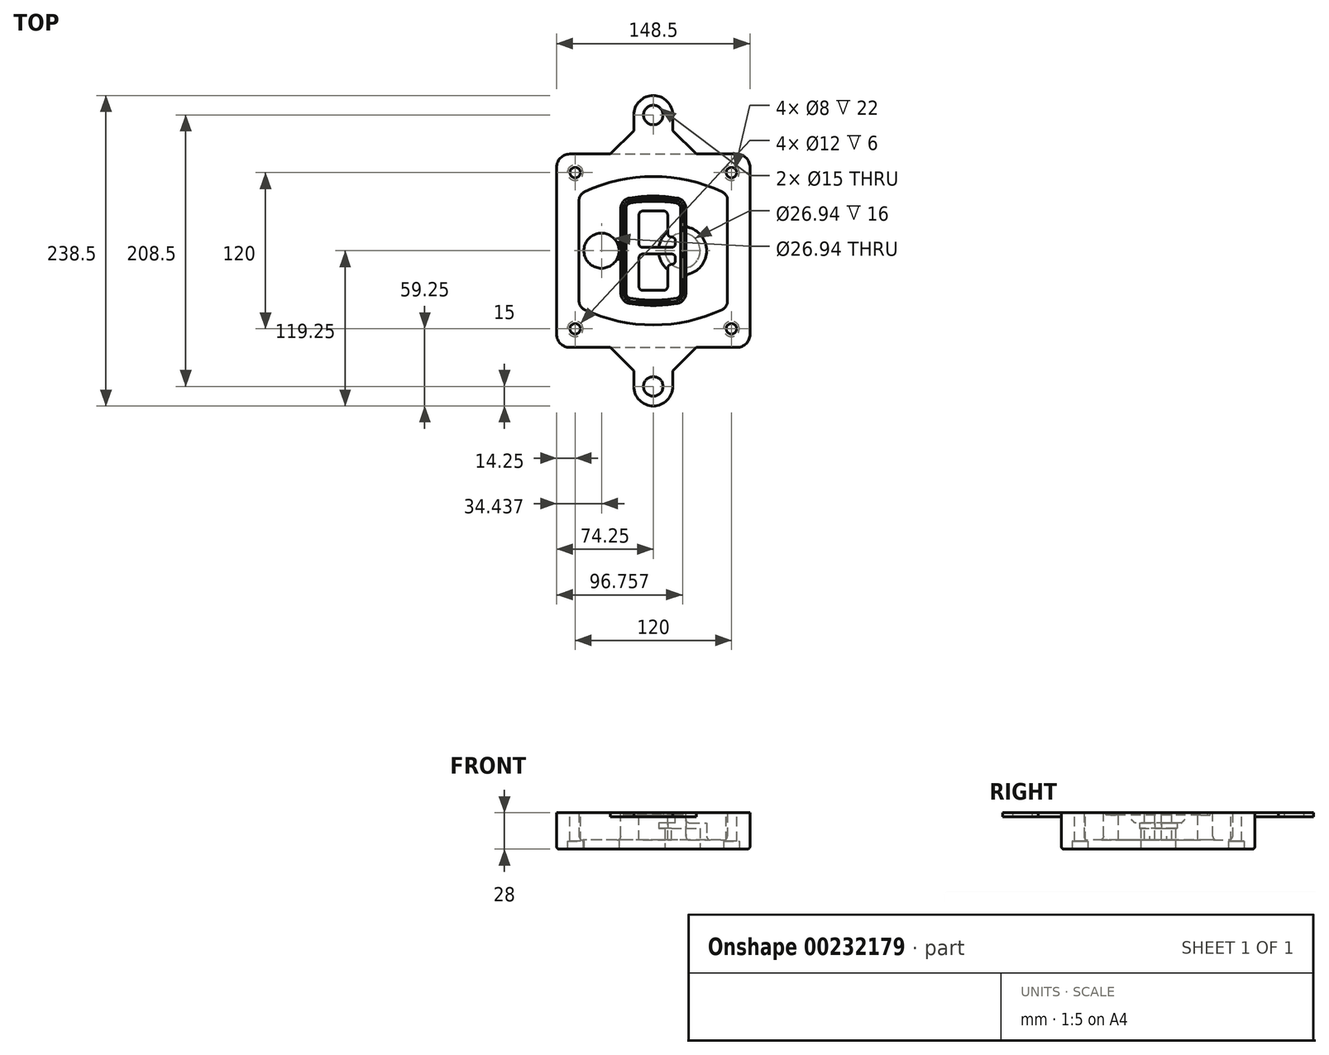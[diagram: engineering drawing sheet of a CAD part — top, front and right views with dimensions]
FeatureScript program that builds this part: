
annotation { "Feature Type Name" : "Feature", "Feature Type Description" : "" }
export const myFeature = defineFeature(function(context is Context, id is Id, definition is map)
    precondition{}
    {
        {
            var Q0;
            Q0=qCreatedBy(makeId("Top.planeOp"),FACE);
            var sketch = newSketch(context, id + "F0", { "sketchPlane" : qUnion([Q0])});
            skPoint(sketch, "E0.rect.middle", {"position": v(0, 0) * mm});
            skLineSegment(sketch, "E1.bottom", {"start": v(-64.25, -74.25) * mm, "end": v(64.25, -74.25) * mm});
            skLineSegment(sketch, "E1.top", {"start": v(-64.25, 74.25) * mm, "end": v(64.25, 74.25) * mm});
            skLineSegment(sketch, "E1.left", {"start": v(-74.25, -64.25) * mm, "end": v(-74.25, 64.25) * mm});
            skLineSegment(sketch, "E1.right", {"start": v(74.25, -64.25) * mm, "end": v(74.25, 64.25) * mm});
            skLineSegment(sketch, "E2", {"start": v(-74.25, 74.25) * mm, "end": v(74.25, -74.25) * mm, "construction": true});
            skLineSegment(sketch, "E3", {"start": v(74.25, 74.25) * mm, "end": v(-74.25, -74.25) * mm, "construction": true});
            skCircle(sketch, "E4", {"center": v(-60, 60) * mm, "radius": 4 * mm});
            skCircle(sketch, "E5", {"center": v(60, 60) * mm, "radius": 4 * mm});
            skCircle(sketch, "E6", {"center": v(60, -60) * mm, "radius": 4 * mm});
            skCircle(sketch, "E7", {"center": v(-60, -60) * mm, "radius": 4 * mm});
            skLineSegment(sketch, "E8", {"start": v(-60, 60) * mm, "end": v(60, 60) * mm, "construction": true});
            skLineSegment(sketch, "E9", {"start": v(60, 60) * mm, "end": v(60, -60) * mm, "construction": true});
            skLineSegment(sketch, "E10", {"start": v(60, -60) * mm, "end": v(-60, -60) * mm, "construction": true});
            skLineSegment(sketch, "E11", {"start": v(-60, -60) * mm, "end": v(-60, 60) * mm, "construction": true});
            skLineSegment(sketch, "E12", {"start": v(-60, 38.83) * mm, "end": v(-60, -38.83) * mm});
            skLineSegment(sketch, "E13", {"start": v(60, 38.83) * mm, "end": v(60, -38.83) * mm});
            skArc(sketch, "E14", {"start": v(54.26, 47.88) * mm, "mid": v(0, 60) * mm, "end": v(-54.26, 47.88) * mm});
            skArc(sketch, "E15", {"start": v(-54.26, -47.88) * mm, "mid": v(0, -60) * mm, "end": v(54.26, -47.88) * mm});
            skLineSegment(sketch, "E16", {"start": v(-60, 0) * mm, "end": v(60, 0) * mm, "construction": true});
            skPoint(sketch, "E17.visualSharp", {"position": v(-60, -45) * mm});
            skArc(sketch, "E17.filletArc", {"start": v(-60, -38.83) * mm, "mid": v(-58.44, -44.2) * mm, "end": v(-54.26, -47.88) * mm});
            skPoint(sketch, "E18.visualSharp", {"position": v(-60, 45) * mm});
            skArc(sketch, "E18.filletArc", {"start": v(-54.26, 47.88) * mm, "mid": v(-58.44, 44.2) * mm, "end": v(-60, 38.83) * mm});
            skPoint(sketch, "E19.visualSharp", {"position": v(60, 45) * mm});
            skArc(sketch, "E19.filletArc", {"start": v(60, 38.83) * mm, "mid": v(58.44, 44.2) * mm, "end": v(54.26, 47.88) * mm});
            skPoint(sketch, "E20.visualSharp", {"position": v(60, -45) * mm});
            skArc(sketch, "E20.filletArc", {"start": v(54.26, -47.88) * mm, "mid": v(58.44, -44.2) * mm, "end": v(60, -38.83) * mm});
            skPoint(sketch, "E21.visualSharp", {"position": v(-74.25, 74.25) * mm});
            skArc(sketch, "E21.filletArc", {"start": v(-64.25, 74.25) * mm, "mid": v(-71.32, 71.32) * mm, "end": v(-74.25, 64.25) * mm});
            skPoint(sketch, "E22.visualSharp", {"position": v(74.25, 74.25) * mm});
            skArc(sketch, "E22.filletArc", {"start": v(74.25, 64.25) * mm, "mid": v(71.32, 71.32) * mm, "end": v(64.25, 74.25) * mm});
            skPoint(sketch, "E23.visualSharp", {"position": v(74.25, -74.25) * mm});
            skArc(sketch, "E23.filletArc", {"start": v(64.25, -74.25) * mm, "mid": v(71.32, -71.32) * mm, "end": v(74.25, -64.25) * mm});
            skPoint(sketch, "E24.visualSharp", {"position": v(-74.25, -74.25) * mm});
            skArc(sketch, "E24.filletArc", {"start": v(-74.25, -64.25) * mm, "mid": v(-71.32, -71.32) * mm, "end": v(-64.25, -74.25) * mm});
            skArc(sketch, "E25.0", {"start": v(57, 38.83) * mm, "mid": v(55.9, 42.58) * mm, "end": v(52.98, 45.17) * mm});
            skLineSegment(sketch, "E25.1", {"start": v(57, 38.83) * mm, "end": v(57, -38.83) * mm});
            skArc(sketch, "E25.2", {"start": v(52.98, -45.17) * mm, "mid": v(55.9, -42.58) * mm, "end": v(57, -38.83) * mm});
            skArc(sketch, "E25.3", {"start": v(-52.98, -45.17) * mm, "mid": v(0, -57) * mm, "end": v(52.98, -45.17) * mm});
            skArc(sketch, "E25.4", {"start": v(-57, -38.83) * mm, "mid": v(-55.9, -42.58) * mm, "end": v(-52.98, -45.17) * mm});
            skArc(sketch, "E25.5", {"start": v(52.98, 45.17) * mm, "mid": v(0, 57) * mm, "end": v(-52.98, 45.17) * mm});
            skLineSegment(sketch, "E25.6", {"start": v(-57, 38.83) * mm, "end": v(-57, -38.83) * mm});
            skArc(sketch, "E25.7", {"start": v(-52.98, 45.17) * mm, "mid": v(-55.9, 42.58) * mm, "end": v(-57, 38.83) * mm});
            skArc(sketch, "E26.0", {"start": v(-55.96, 51.5) * mm, "mid": v(-61.82, 46.33) * mm, "end": v(-64, 38.83) * mm});
            skArc(sketch, "E26.1", {"start": v(55.96, 51.5) * mm, "mid": v(0, 64) * mm, "end": v(-55.96, 51.5) * mm});
            skArc(sketch, "E26.2", {"start": v(64, 38.83) * mm, "mid": v(61.82, 46.33) * mm, "end": v(55.96, 51.5) * mm});
            skLineSegment(sketch, "E26.3", {"start": v(64, 38.83) * mm, "end": v(64, -38.83) * mm});
            skArc(sketch, "E26.4", {"start": v(55.96, -51.5) * mm, "mid": v(61.82, -46.33) * mm, "end": v(64, -38.83) * mm});
            skLineSegment(sketch, "E26.5", {"start": v(-64, 38.83) * mm, "end": v(-64, -38.83) * mm});
            skArc(sketch, "E26.6", {"start": v(-55.96, -51.5) * mm, "mid": v(0, -64) * mm, "end": v(55.96, -51.5) * mm});
            skArc(sketch, "E26.7", {"start": v(-64, -38.83) * mm, "mid": v(-61.82, -46.33) * mm, "end": v(-55.96, -51.5) * mm});
            skSolve(sketch);
        }
        {
            var Q0;
            Q0=makeQuery(id+"F0.imprint","IMPRINT",FACE,{"disambiguationData":[TD([[makeQuery(id+"F0.imprint","IMPRINT",EDGE,{"derivedFrom":sQuery(id+"F0.wireOp",EDGE,"E1.bottom")}),1.0]])]});
            var Q1;
            Q1=makeQuery(id+"F0.imprint","IMPRINT",FACE,{"disambiguationData":[TD([[makeQuery(id+"F0.imprint","IMPRINT",EDGE,{"derivedFrom":sQuery(id+"F0.wireOp",EDGE,"E12")}),1.0]])]});
            var Q2;
            Q2=makeQuery(id+"F0.imprint","IMPRINT",FACE,{"disambiguationData":[TD([[makeQuery(id+"F0.imprint","IMPRINT",EDGE,{"derivedFrom":sQuery(id+"F0.wireOp",EDGE,"E25.0")}),1.0]])]});
            var Q3;
            Q3=makeQuery(id+"F0.imprint","IMPRINT",FACE,{"disambiguationData":[TD([[makeQuery(id+"F0.imprint","IMPRINT",EDGE,{"derivedFrom":sQuery(id+"F0.wireOp",EDGE,"E12")}),-1.0]])]});
            extrude(context, id + "F1", {"entities" : qUnion([Q0, Q1, Q2, Q3]), "oppositeDirection" : true, "depth" : 25 * mm});
        }
        {
            var Q0;
            Q0=makeQuery(id+"F0.imprint","IMPRINT",FACE,{"disambiguationData":[TD([[makeQuery(id+"F0.imprint","IMPRINT",EDGE,{"derivedFrom":sQuery(id+"F0.wireOp",EDGE,"E12")}),1.0]])]});
            extrude(context, id + "F2", {"entities" : qUnion([Q0]), "operationType" : NewBodyOperationType.ADD, "depth" : 3 * mm});
        }
        {
            var Q0;
            Q0=makeQuery(id+"F0.imprint","IMPRINT",FACE,{"disambiguationData":[TD([[makeQuery(id+"F0.imprint","IMPRINT",EDGE,{"derivedFrom":sQuery(id+"F0.wireOp",EDGE,"E25.0")}),1.0]])]});
            extrude(context, id + "F3", {"entities" : qUnion([Q0]), "operationType" : NewBodyOperationType.REMOVE, "oppositeDirection" : true, "depth" : 18 * mm});
        }
        {
            var Q0;
            Q0=makeQuery(id+"F2.opExtrude","CAP_FACE",FACE,{"disambiguationData":[OSD([sQuery(id+"F0.wireOp",EDGE,"E12"),sQuery(id+"F0.wireOp",EDGE,"E13"),sQuery(id+"F0.wireOp",EDGE,"E14"),sQuery(id+"F0.wireOp",EDGE,"E15"),sQuery(id+"F0.wireOp",EDGE,"E17.filletArc"),sQuery(id+"F0.wireOp",EDGE,"E18.filletArc"),sQuery(id+"F0.wireOp",EDGE,"E19.filletArc"),sQuery(id+"F0.wireOp",EDGE,"E20.filletArc"),sQuery(id+"F0.wireOp",EDGE,"E25.0"),sQuery(id+"F0.wireOp",EDGE,"E25.1"),sQuery(id+"F0.wireOp",EDGE,"E25.2"),sQuery(id+"F0.wireOp",EDGE,"E25.3"),sQuery(id+"F0.wireOp",EDGE,"E25.4"),sQuery(id+"F0.wireOp",EDGE,"E25.5"),sQuery(id+"F0.wireOp",EDGE,"E25.6"),sQuery(id+"F0.wireOp",EDGE,"E25.7")])],"isStart":false});
            var sketch = newSketch(context, id + "F4", { "sketchPlane" : qUnion([Q0])});
            skArc(sketch, "E27.0", {"start": v(-18.34, -40.45) * mm, "mid": v(0, -42) * mm, "end": v(18.34, -40.45) * mm});
            skArc(sketch, "E28.0", {"start": v(18.34, 40.45) * mm, "mid": v(0, 42) * mm, "end": v(-18.34, 40.45) * mm});
            skLineSegment(sketch, "E29", {"start": v(-25, 32.57) * mm, "end": v(-25, -32.57) * mm});
            skLineSegment(sketch, "E30", {"start": v(25, 32.57) * mm, "end": v(25, -32.57) * mm});
            skLineSegment(sketch, "E31", {"start": v(-25, 39.1) * mm, "end": v(25, 39.1) * mm, "construction": true});
            skLineSegment(sketch, "E32", {"start": v(-25, -39.1) * mm, "end": v(25, -39.1) * mm, "construction": true});
            skPoint(sketch, "E33.visualSharp", {"position": v(-25, 39.1) * mm});
            skArc(sketch, "E33.filletArc", {"start": v(-18.34, 40.45) * mm, "mid": v(-23.11, 37.73) * mm, "end": v(-25, 32.57) * mm});
            skPoint(sketch, "E34.visualSharp", {"position": v(25, 39.1) * mm});
            skArc(sketch, "E34.filletArc", {"start": v(25, 32.57) * mm, "mid": v(23.11, 37.73) * mm, "end": v(18.34, 40.45) * mm});
            skPoint(sketch, "E35.visualSharp", {"position": v(25, -39.1) * mm});
            skArc(sketch, "E35.filletArc", {"start": v(18.34, -40.45) * mm, "mid": v(23.11, -37.73) * mm, "end": v(25, -32.57) * mm});
            skPoint(sketch, "E36.visualSharp", {"position": v(-25, -39.1) * mm});
            skArc(sketch, "E36.filletArc", {"start": v(-25, -32.57) * mm, "mid": v(-23.11, -37.73) * mm, "end": v(-18.34, -40.45) * mm});
            skArc(sketch, "E37.0", {"start": v(52.98, 45.17) * mm, "mid": v(0, 57) * mm, "end": v(-52.98, 45.17) * mm});
            skArc(sketch, "E37.1", {"start": v(-52.98, 45.17) * mm, "mid": v(-55.9, 42.58) * mm, "end": v(-57, 38.83) * mm});
            skLineSegment(sketch, "E37.2", {"start": v(-57, 38.83) * mm, "end": v(-57, -38.83) * mm});
            skArc(sketch, "E37.3", {"start": v(-57, -38.83) * mm, "mid": v(-55.9, -42.58) * mm, "end": v(-52.98, -45.17) * mm});
            skArc(sketch, "E37.4", {"start": v(-52.98, -45.17) * mm, "mid": v(0, -57) * mm, "end": v(52.98, -45.17) * mm});
            skArc(sketch, "E37.5", {"start": v(52.98, -45.17) * mm, "mid": v(55.9, -42.58) * mm, "end": v(57, -38.83) * mm});
            skLineSegment(sketch, "E37.6", {"start": v(57, 38.83) * mm, "end": v(57, -38.83) * mm});
            skArc(sketch, "E37.7", {"start": v(57, 38.83) * mm, "mid": v(55.9, 42.58) * mm, "end": v(52.98, 45.17) * mm});
            skLineSegment(sketch, "E38.0", {"start": v(23, 32.57) * mm, "end": v(23, -32.57) * mm});
            skArc(sketch, "E38.1", {"start": v(18, -38.48) * mm, "mid": v(21.58, -36.44) * mm, "end": v(23, -32.57) * mm});
            skArc(sketch, "E38.2", {"start": v(-18, -38.48) * mm, "mid": v(0, -40) * mm, "end": v(18, -38.48) * mm});
            skArc(sketch, "E38.3", {"start": v(-23, -32.57) * mm, "mid": v(-21.58, -36.44) * mm, "end": v(-18, -38.48) * mm});
            skLineSegment(sketch, "E38.4", {"start": v(-23, 32.57) * mm, "end": v(-23, -32.57) * mm});
            skArc(sketch, "E38.5", {"start": v(23, 32.57) * mm, "mid": v(21.58, 36.44) * mm, "end": v(18, 38.48) * mm});
            skArc(sketch, "E38.6", {"start": v(-18, 38.48) * mm, "mid": v(-21.58, 36.44) * mm, "end": v(-23, 32.57) * mm});
            skArc(sketch, "E38.7", {"start": v(18, 38.48) * mm, "mid": v(0, 40) * mm, "end": v(-18, 38.48) * mm});
            skArc(sketch, "E39.0", {"start": v(21, 32.57) * mm, "mid": v(20.06, 35.15) * mm, "end": v(17.67, 36.5) * mm});
            skLineSegment(sketch, "E39.1", {"start": v(21, 32.57) * mm, "end": v(21, -32.57) * mm});
            skArc(sketch, "E39.2", {"start": v(17.67, -36.5) * mm, "mid": v(20.06, -35.15) * mm, "end": v(21, -32.57) * mm});
            skArc(sketch, "E39.3", {"start": v(-17.67, -36.5) * mm, "mid": v(0, -38) * mm, "end": v(17.67, -36.5) * mm});
            skArc(sketch, "E39.4", {"start": v(-21, -32.57) * mm, "mid": v(-20.06, -35.15) * mm, "end": v(-17.67, -36.5) * mm});
            skArc(sketch, "E39.5", {"start": v(17.67, 36.5) * mm, "mid": v(0, 38) * mm, "end": v(-17.67, 36.5) * mm});
            skLineSegment(sketch, "E39.6", {"start": v(-21, 32.57) * mm, "end": v(-21, -32.57) * mm});
            skArc(sketch, "E39.7", {"start": v(-17.67, 36.5) * mm, "mid": v(-20.06, 35.15) * mm, "end": v(-21, 32.57) * mm});
            skLineSegment(sketch, "E40", {"start": v(-25, 0) * mm, "end": v(25, 0) * mm, "construction": true});
            skLineSegment(sketch, "E41", {"start": v(-11, 5.5) * mm, "end": v(-11, 27.5) * mm});
            skLineSegment(sketch, "E42", {"start": v(-8, 30.5) * mm, "end": v(8, 30.5) * mm});
            skLineSegment(sketch, "E43", {"start": v(11, 27.5) * mm, "end": v(11, 13.5) * mm});
            skLineSegment(sketch, "E44", {"start": v(14, 10.5) * mm, "end": v(14, 10.5) * mm});
            skLineSegment(sketch, "E45", {"start": v(17, 7.5) * mm, "end": v(17, 5.5) * mm});
            skLineSegment(sketch, "E46", {"start": v(14, 2.5) * mm, "end": v(-8, 2.5) * mm});
            skPoint(sketch, "E47.visualSharp", {"position": v(-11, 30.5) * mm});
            skArc(sketch, "E47.filletArc", {"start": v(-8, 30.5) * mm, "mid": v(-10.12, 29.62) * mm, "end": v(-11, 27.5) * mm});
            skPoint(sketch, "E48.visualSharp", {"position": v(11, 30.5) * mm});
            skArc(sketch, "E48.filletArc", {"start": v(11, 27.5) * mm, "mid": v(10.12, 29.62) * mm, "end": v(8, 30.5) * mm});
            skPoint(sketch, "E49.visualSharp", {"position": v(11, 10.5) * mm});
            skArc(sketch, "E49.filletArc", {"start": v(11, 13.5) * mm, "mid": v(11.88, 11.38) * mm, "end": v(14, 10.5) * mm});
            skPoint(sketch, "E50.visualSharp", {"position": v(17, 10.5) * mm});
            skArc(sketch, "E50.filletArc", {"start": v(17, 7.5) * mm, "mid": v(16.12, 9.62) * mm, "end": v(14, 10.5) * mm});
            skPoint(sketch, "E51.visualSharp", {"position": v(17, 2.5) * mm});
            skArc(sketch, "E51.filletArc", {"start": v(14, 2.5) * mm, "mid": v(16.12, 3.38) * mm, "end": v(17, 5.5) * mm});
            skPoint(sketch, "E52.visualSharp", {"position": v(-11, 2.5) * mm});
            skArc(sketch, "E52.filletArc", {"start": v(-11, 5.5) * mm, "mid": v(-10.12, 3.38) * mm, "end": v(-8, 2.5) * mm});
            skLineSegment(sketch, "E53.0.MirrorCS", {"start": v(14, -2.5) * mm, "end": v(-8, -2.5) * mm});
            skArc(sketch, "E54.0.MirrorCS", {"start": v(-11, -5.5) * mm, "mid": v(-10.12, -3.38) * mm, "end": v(-8, -2.5) * mm});
            skLineSegment(sketch, "E55.0.MirrorCS", {"start": v(-11, -5.5) * mm, "end": v(-11, -27.5) * mm});
            skArc(sketch, "E56.0.MirrorCS", {"start": v(-8, -30.5) * mm, "mid": v(-10.12, -29.62) * mm, "end": v(-11, -27.5) * mm});
            skLineSegment(sketch, "E57.0.MirrorCS", {"start": v(-8, -30.5) * mm, "end": v(8, -30.5) * mm});
            skArc(sketch, "E58.0.MirrorCS", {"start": v(11, -27.5) * mm, "mid": v(10.12, -29.62) * mm, "end": v(8, -30.5) * mm});
            skLineSegment(sketch, "E59.0.MirrorCS", {"start": v(11, -27.5) * mm, "end": v(11, -13.5) * mm});
            skArc(sketch, "E60.0.MirrorCS", {"start": v(11, -13.5) * mm, "mid": v(11.88, -11.38) * mm, "end": v(14, -10.5) * mm});
            skArc(sketch, "E61.0.MirrorCS", {"start": v(17, -7.5) * mm, "mid": v(16.12, -9.62) * mm, "end": v(14, -10.5) * mm});
            skLineSegment(sketch, "E62.0.MirrorCS", {"start": v(17, -7.5) * mm, "end": v(17, -5.5) * mm});
            skArc(sketch, "E63.0.MirrorCS", {"start": v(14, -2.5) * mm, "mid": v(16.12, -3.38) * mm, "end": v(17, -5.5) * mm});
            skSolve(sketch);
        }
        {
            var Q0;
            Q0=makeQuery(id+"F4.imprint","IMPRINT",FACE,{"disambiguationData":[TD([[makeQuery(id+"F4.imprint","IMPRINT",EDGE,{"derivedFrom":sQuery(id+"F4.wireOp",EDGE,"E27.0")}),1.0]])]});
            var Q1;
            Q1=makeQuery(id+"F4.imprint","IMPRINT",FACE,{"disambiguationData":[TD([[makeQuery(id+"F4.imprint","IMPRINT",EDGE,{"derivedFrom":sQuery(id+"F4.wireOp",EDGE,"E38.0")}),-1.0]])]});
            var Q2;
            Q2=makeQuery(id+"F4.imprint","IMPRINT",FACE,{"disambiguationData":[TD([[makeQuery(id+"F4.imprint","IMPRINT",EDGE,{"derivedFrom":sQuery(id+"F4.wireOp",EDGE,"E39.0")}),1.0]])]});
            extrude(context, id + "F5", {"entities" : qUnion([Q0, Q1, Q2]), "operationType" : NewBodyOperationType.ADD, "endBound" : BoundingType.UP_TO_NEXT, "oppositeDirection" : true, "depth" : 25 * mm});
        }
        {
            var Q0;
            Q0=makeQuery(id+"F4.imprint","IMPRINT",FACE,{"disambiguationData":[TD([[makeQuery(id+"F4.imprint","IMPRINT",EDGE,{"derivedFrom":sQuery(id+"F4.wireOp",EDGE,"E38.0")}),-1.0]])]});
            extrude(context, id + "F6", {"entities" : qUnion([Q0]), "operationType" : NewBodyOperationType.REMOVE, "oppositeDirection" : true, "depth" : 2 * mm});
        }
        {
            var Q0;
            Q0=makeQuery(id+"F1.opExtrude","CAP_FACE",FACE,{"disambiguationData":[OSD([sQuery(id+"F0.wireOp",EDGE,"E1.bottom"),sQuery(id+"F0.wireOp",EDGE,"E1.top"),sQuery(id+"F0.wireOp",EDGE,"E1.left"),sQuery(id+"F0.wireOp",EDGE,"E1.right"),sQuery(id+"F0.wireOp",EDGE,"E4"),sQuery(id+"F0.wireOp",EDGE,"E5"),sQuery(id+"F0.wireOp",EDGE,"E6"),sQuery(id+"F0.wireOp",EDGE,"E7"),sQuery(id+"F0.wireOp",EDGE,"E21.filletArc"),sQuery(id+"F0.wireOp",EDGE,"E22.filletArc"),sQuery(id+"F0.wireOp",EDGE,"E23.filletArc"),sQuery(id+"F0.wireOp",EDGE,"E24.filletArc")])],"isStart":false});
            var sketch = newSketch(context, id + "F7", { "sketchPlane" : qUnion([Q0])});
            skCircle(sketch, "E64", {"center": v(22.5, 0) * mm, "radius": 13.47 * mm});
            skCircle(sketch, "E65", {"center": v(-39.81, 0) * mm, "radius": 13.47 * mm});
            skLineSegment(sketch, "E66", {"start": v(74.25, 0) * mm, "end": v(-74.25, 0) * mm});
            skCircle(sketch, "E67", {"center": v(22.5, 0) * mm, "radius": 18.47 * mm});
            skCircle(sketch, "E68", {"center": v(60, -60) * mm, "radius": 6 * mm});
            skCircle(sketch, "E69", {"center": v(-60, -60) * mm, "radius": 6 * mm});
            skCircle(sketch, "E70", {"center": v(-60, 60) * mm, "radius": 6 * mm});
            skCircle(sketch, "E71", {"center": v(60, 60) * mm, "radius": 6 * mm});
            skSolve(sketch);
        }
        {
            var Q0;
            {var subQ1=sQuery(id+"F7.wireOp",EDGE,"E66");var subQ4=sQuery(id+"F7.wireOp",EDGE,"E64");var subQ6=makeQuery(id+"F7.imprint","INTERSECT",VERTEX,{"disambiguationData":[OD(0.0)],"derivedFrom":[subQ4,subQ1]});Q0=makeQuery(id+"F7.imprint","IMPRINT",FACE,{"disambiguationData":[TD([[makeQuery(id+"F7.imprint","IMPRINT",EDGE,{"disambiguationData":[TD([[subQ6,-1.0]])],"derivedFrom":subQ4}),-1.0]])]});}
            var Q1;
            {var subQ0=sQuery(id+"F7.wireOp",EDGE,"E66");var subQ1=sQuery(id+"F7.wireOp",EDGE,"E64");var subQ3=makeQuery(id+"F7.imprint","INTERSECT",VERTEX,{"disambiguationData":[OD(0.0)],"derivedFrom":[subQ1,subQ0]});Q1=makeQuery(id+"F7.imprint","IMPRINT",FACE,{"disambiguationData":[TD([[makeQuery(id+"F7.imprint","IMPRINT",EDGE,{"disambiguationData":[TD([[subQ3,-1.0]])],"derivedFrom":subQ1}),1.0]])]});}
            var Q2;
            {var subQ0=sQuery(id+"F7.wireOp",EDGE,"E66");var subQ1=sQuery(id+"F7.wireOp",EDGE,"E64");var subQ3=makeQuery(id+"F7.imprint","INTERSECT",VERTEX,{"disambiguationData":[OD(0.0)],"derivedFrom":[subQ1,subQ0]});Q2=makeQuery(id+"F7.imprint","IMPRINT",FACE,{"disambiguationData":[TD([[makeQuery(id+"F7.imprint","IMPRINT",EDGE,{"disambiguationData":[TD([[subQ3,1.0]])],"derivedFrom":subQ1}),1.0]])]});}
            var Q3;
            {var subQ1=sQuery(id+"F7.wireOp",EDGE,"E66");var subQ4=sQuery(id+"F7.wireOp",EDGE,"E64");var subQ6=makeQuery(id+"F7.imprint","INTERSECT",VERTEX,{"disambiguationData":[OD(0.0)],"derivedFrom":[subQ4,subQ1]});Q3=makeQuery(id+"F7.imprint","IMPRINT",FACE,{"disambiguationData":[TD([[makeQuery(id+"F7.imprint","IMPRINT",EDGE,{"disambiguationData":[TD([[subQ6,1.0]])],"derivedFrom":subQ4}),-1.0]])]});}
            extrude(context, id + "F8", {"entities" : qUnion([Q0, Q1, Q2, Q3]), "operationType" : NewBodyOperationType.ADD, "oppositeDirection" : true, "depth" : 20 * mm});
        }
        {
            var Q0;
            {var subQ0=sQuery(id+"F7.wireOp",EDGE,"E66");var subQ1=sQuery(id+"F7.wireOp",EDGE,"E64");var subQ3=makeQuery(id+"F7.imprint","INTERSECT",VERTEX,{"disambiguationData":[OD(0.0)],"derivedFrom":[subQ1,subQ0]});Q0=makeQuery(id+"F7.imprint","IMPRINT",FACE,{"disambiguationData":[TD([[makeQuery(id+"F7.imprint","IMPRINT",EDGE,{"disambiguationData":[TD([[subQ3,-1.0]])],"derivedFrom":subQ1}),1.0]])]});}
            var Q1;
            {var subQ0=sQuery(id+"F7.wireOp",EDGE,"E66");var subQ1=sQuery(id+"F7.wireOp",EDGE,"E64");var subQ3=makeQuery(id+"F7.imprint","INTERSECT",VERTEX,{"disambiguationData":[OD(0.0)],"derivedFrom":[subQ1,subQ0]});Q1=makeQuery(id+"F7.imprint","IMPRINT",FACE,{"disambiguationData":[TD([[makeQuery(id+"F7.imprint","IMPRINT",EDGE,{"disambiguationData":[TD([[subQ3,1.0]])],"derivedFrom":subQ1}),1.0]])]});}
            extrude(context, id + "F9", {"entities" : qUnion([Q0, Q1]), "operationType" : NewBodyOperationType.REMOVE, "oppositeDirection" : true, "depth" : 16 * mm});
        }
        {
            var Q0;
            {var subQ0=sQuery(id+"F7.wireOp",EDGE,"E66");var subQ1=sQuery(id+"F7.wireOp",EDGE,"E65");var subQ3=makeQuery(id+"F7.imprint","INTERSECT",VERTEX,{"disambiguationData":[OD(0.0)],"derivedFrom":[subQ1,subQ0]});Q0=makeQuery(id+"F7.imprint","IMPRINT",FACE,{"disambiguationData":[TD([[makeQuery(id+"F7.imprint","IMPRINT",EDGE,{"disambiguationData":[TD([[subQ3,-1.0]])],"derivedFrom":subQ1}),1.0]])]});}
            var Q1;
            {var subQ0=sQuery(id+"F7.wireOp",EDGE,"E66");var subQ1=sQuery(id+"F7.wireOp",EDGE,"E65");var subQ3=makeQuery(id+"F7.imprint","INTERSECT",VERTEX,{"disambiguationData":[OD(0.0)],"derivedFrom":[subQ1,subQ0]});Q1=makeQuery(id+"F7.imprint","IMPRINT",FACE,{"disambiguationData":[TD([[makeQuery(id+"F7.imprint","IMPRINT",EDGE,{"disambiguationData":[TD([[subQ3,1.0]])],"derivedFrom":subQ1}),1.0]])]});}
            extrude(context, id + "F10", {"entities" : qUnion([Q0, Q1]), "operationType" : NewBodyOperationType.REMOVE, "oppositeDirection" : true, "depth" : 25 * mm});
        }
        {
            var Q0;
            Q0=makeQuery(id+"F7.imprint","IMPRINT",FACE,{"disambiguationData":[TD([[makeQuery(id+"F7.imprint","IMPRINT",EDGE,{"derivedFrom":sQuery(id+"F7.wireOp",EDGE,"E68")}),1.0]])]});
            var Q1;
            Q1=makeQuery(id+"F7.imprint","IMPRINT",FACE,{"disambiguationData":[TD([[makeQuery(id+"F7.imprint","IMPRINT",EDGE,{"derivedFrom":makeQuery(id+"F1.opExtrude","CAP_EDGE",EDGE,{"disambiguationData":[OSD([sQuery(id+"F0.wireOp",EDGE,"E5")])],"isStart":false})}),-1.0]])]});
            var Q2;
            Q2=makeQuery(id+"F7.imprint","IMPRINT",FACE,{"disambiguationData":[TD([[makeQuery(id+"F7.imprint","IMPRINT",EDGE,{"derivedFrom":sQuery(id+"F7.wireOp",EDGE,"E69")}),1.0]])]});
            var Q3;
            Q3=makeQuery(id+"F7.imprint","IMPRINT",FACE,{"disambiguationData":[TD([[makeQuery(id+"F7.imprint","IMPRINT",EDGE,{"derivedFrom":makeQuery(id+"F1.opExtrude","CAP_EDGE",EDGE,{"disambiguationData":[OSD([sQuery(id+"F0.wireOp",EDGE,"E4")])],"isStart":false})}),-1.0]])]});
            var Q4;
            Q4=makeQuery(id+"F7.imprint","IMPRINT",FACE,{"disambiguationData":[TD([[makeQuery(id+"F7.imprint","IMPRINT",EDGE,{"derivedFrom":sQuery(id+"F7.wireOp",EDGE,"E70")}),1.0]])]});
            var Q5;
            Q5=makeQuery(id+"F7.imprint","IMPRINT",FACE,{"disambiguationData":[TD([[makeQuery(id+"F7.imprint","IMPRINT",EDGE,{"derivedFrom":makeQuery(id+"F1.opExtrude","CAP_EDGE",EDGE,{"disambiguationData":[OSD([sQuery(id+"F0.wireOp",EDGE,"E7")])],"isStart":false})}),-1.0]])]});
            var Q6;
            Q6=makeQuery(id+"F7.imprint","IMPRINT",FACE,{"disambiguationData":[TD([[makeQuery(id+"F7.imprint","IMPRINT",EDGE,{"derivedFrom":sQuery(id+"F7.wireOp",EDGE,"E71")}),1.0]])]});
            var Q7;
            Q7=makeQuery(id+"F7.imprint","IMPRINT",FACE,{"disambiguationData":[TD([[makeQuery(id+"F7.imprint","IMPRINT",EDGE,{"derivedFrom":makeQuery(id+"F1.opExtrude","CAP_EDGE",EDGE,{"disambiguationData":[OSD([sQuery(id+"F0.wireOp",EDGE,"E6")])],"isStart":false})}),-1.0]])]});
            extrude(context, id + "F11", {"entities" : qUnion([Q0, Q1, Q2, Q3, Q4, Q5, Q6, Q7]), "operationType" : NewBodyOperationType.REMOVE, "oppositeDirection" : true, "depth" : 6 * mm});
        }
        {
            var Q0;
            Q0=makeQuery(id+"F9.boolean.opBoolean","COPY",FACE,{"derivedFrom":makeQuery(id+"F9.opExtrude","CAP_FACE",FACE,{"disambiguationData":[OSD([sQuery(id+"F7.wireOp",EDGE,"E64")])],"isStart":false})});
            var sketch = newSketch(context, id + "F12", { "sketchPlane" : qUnion([Q0])});
            skArc(sketch, "E72.0", {"start": v(11, 14.45) * mm, "mid": v(6.45, 9.13) * mm, "end": v(4.2, 2.5) * mm});
            skArc(sketch, "E72.1", {"start": v(4.2, -2.5) * mm, "mid": v(6.45, -9.13) * mm, "end": v(11, -14.45) * mm});
            skLineSegment(sketch, "E73", {"start": v(4.2, -2.5) * mm, "end": v(14, -2.5) * mm});
            skLineSegment(sketch, "E74.0", {"start": v(14, 2.5) * mm, "end": v(4.2, 2.5) * mm});
            skArc(sketch, "E74.1", {"start": v(14, 2.5) * mm, "mid": v(16.12, 3.38) * mm, "end": v(17, 5.5) * mm});
            skLineSegment(sketch, "E74.2", {"start": v(17, 7.5) * mm, "end": v(17, 5.5) * mm});
            skArc(sketch, "E74.3", {"start": v(17, 7.5) * mm, "mid": v(16.12, 9.62) * mm, "end": v(14, 10.5) * mm});
            skArc(sketch, "E74.4", {"start": v(11, 13.5) * mm, "mid": v(11.88, 11.38) * mm, "end": v(14, 10.5) * mm});
            skLineSegment(sketch, "E74.5", {"start": v(11, 14.45) * mm, "end": v(11, 13.5) * mm});
            skLineSegment(sketch, "E74.7", {"start": v(14, -2.5) * mm, "end": v(4.2, -2.5) * mm});
            skArc(sketch, "E74.8", {"start": v(14, -2.5) * mm, "mid": v(16.12, -3.38) * mm, "end": v(17, -5.5) * mm});
            skLineSegment(sketch, "E74.9", {"start": v(17, -7.5) * mm, "end": v(17, -5.5) * mm});
            skArc(sketch, "E74.10", {"start": v(17, -7.5) * mm, "mid": v(16.12, -9.62) * mm, "end": v(14, -10.5) * mm});
            skArc(sketch, "E74.11", {"start": v(11, -13.5) * mm, "mid": v(11.88, -11.38) * mm, "end": v(14, -10.5) * mm});
            skLineSegment(sketch, "E74.12", {"start": v(11, -14.45) * mm, "end": v(11, -13.5) * mm});
            skPoint(sketch, "E75.orphan", {"position": v(11, -27.5) * mm});
            skPoint(sketch, "E76.orphan", {"position": v(-8, -2.5) * mm});
            skPoint(sketch, "E77.orphan", {"position": v(-8, 2.5) * mm});
            skPoint(sketch, "E78.orphan", {"position": v(11, 27.5) * mm});
            skSolve(sketch);
        }
        {
            var Q0;
            {var subQ7=sQuery(id+"F12.wireOp",EDGE,"E72.0");var subQ14=sQuery(id+"F12.wireOp",EDGE,"E72.1");var subQ16=sQuery(id+"F12.wireOp",EDGE,"E74.1");var subQ18=sQuery(id+"F12.wireOp",EDGE,"E74.8");Q0=qUnion([makeQuery(id+"F12.imprint","IMPRINT",FACE,{"disambiguationData":[TD([[makeQuery(id+"F12.imprint","IMPRINT",EDGE,{"derivedFrom":subQ7}),1.0]])]}),makeQuery(id+"F12.imprint","IMPRINT",FACE,{"disambiguationData":[TD([[makeQuery(id+"F12.imprint","IMPRINT",EDGE,{"derivedFrom":subQ14}),1.0]])]}),makeQuery(id+"F12.imprint","IMPRINT",FACE,{"disambiguationData":[TD([[makeQuery(id+"F12.imprint","IMPRINT",EDGE,{"derivedFrom":subQ16}),1.0]])]}),makeQuery(id+"F12.imprint","IMPRINT",FACE,{"disambiguationData":[TD([[makeQuery(id+"F12.imprint","IMPRINT",EDGE,{"derivedFrom":subQ18}),-1.0]])]})]);}
            var Q1;
            Q1=makeQuery(id+"F5.boolean.opBoolean","SPLIT",FACE,{"disambiguationData":[TD([makeQuery(id+"F5.opExtrude","SWEPT_FACE",FACE,{"disambiguationData":[OSD([sQuery(id+"F4.wireOp",EDGE,"E41")])]})])],"derivedFrom":makeQuery(id+"F3.boolean.opBoolean","COPY",FACE,{"derivedFrom":makeQuery(id+"F3.opExtrude","CAP_FACE",FACE,{"disambiguationData":[OSD([sQuery(id+"F0.wireOp",EDGE,"E25.0"),sQuery(id+"F0.wireOp",EDGE,"E25.1"),sQuery(id+"F0.wireOp",EDGE,"E25.2"),sQuery(id+"F0.wireOp",EDGE,"E25.3"),sQuery(id+"F0.wireOp",EDGE,"E25.4"),sQuery(id+"F0.wireOp",EDGE,"E25.5"),sQuery(id+"F0.wireOp",EDGE,"E25.6"),sQuery(id+"F0.wireOp",EDGE,"E25.7")])],"isStart":false})})});
            extrude(context, id + "F13", {"entities" : qUnion([Q0]), "operationType" : NewBodyOperationType.REMOVE, "endBound" : BoundingType.UP_TO_SURFACE, "endBoundEntityFace" : qUnion([Q1]), "depth" : 25 * mm});
        }
        {
            var Q0;
            Q0=makeQuery(id+"F3.boolean.opBoolean","COPY",EDGE,{"derivedFrom":makeQuery(id+"F3.opExtrude","CAP_EDGE",EDGE,{"disambiguationData":[OSD([sQuery(id+"F0.wireOp",EDGE,"E25.6")])],"isStart":false})});
            var Q1;
            Q1=makeQuery(id+"F8.boolean.opBoolean","INTERSECT",EDGE,{"derivedFrom":[makeQuery(id+"F5.opExtrude","SWEPT_FACE",FACE,{"disambiguationData":[OSD([sQuery(id+"F4.wireOp",EDGE,"E30")])]}),makeQuery(id+"F8.opExtrude","CAP_FACE",FACE,{"disambiguationData":[OSD([sQuery(id+"F7.wireOp",EDGE,"E67")])],"isStart":false})]});
            var Q2;
            Q2=makeQuery(id+"F8.boolean.opBoolean","INTERSECT",EDGE,{"disambiguationData":[OD(1.0)],"derivedFrom":[makeQuery(id+"F5.opExtrude","SWEPT_FACE",FACE,{"disambiguationData":[OSD([sQuery(id+"F4.wireOp",EDGE,"E30")])]}),makeQuery(id+"F8.opExtrude","SWEPT_FACE",FACE,{"disambiguationData":[OSD([sQuery(id+"F7.wireOp",EDGE,"E67")])]})]});
            var Q3;
            {var subQ0=sQuery(id+"F4.wireOp",EDGE,"E30");Q3=makeQuery(id+"F8.boolean.opBoolean","SPLIT",EDGE,{"disambiguationData":[TD([makeQuery(id+"F5.opExtrude","SWEPT_FACE",FACE,{"disambiguationData":[OSD([sQuery(id+"F4.wireOp",EDGE,"E35.filletArc")])]})])],"derivedFrom":makeQuery(id+"F5.opExtrude","CAP_EDGE",EDGE,{"disambiguationData":[OSD([subQ0])],"isStart":false})});}
            var Q4;
            {var subQ0=sQuery(id+"F0.wireOp",EDGE,"E25.7");var subQ1=sQuery(id+"F0.wireOp",EDGE,"E25.1");var subQ2=sQuery(id+"F0.wireOp",EDGE,"E25.6");var subQ3=sQuery(id+"F0.wireOp",EDGE,"E25.5");var subQ4=sQuery(id+"F0.wireOp",EDGE,"E25.4");var subQ5=sQuery(id+"F0.wireOp",EDGE,"E25.0");var subQ6=sQuery(id+"F0.wireOp",EDGE,"E25.2");var subQ7=sQuery(id+"F0.wireOp",EDGE,"E25.3");Q4=makeQuery(id+"F8.boolean.opBoolean","INTERSECT",EDGE,{"derivedFrom":[makeQuery(id+"F5.boolean.opBoolean","SPLIT",FACE,{"disambiguationData":[TD([makeQuery(id+"F2.opExtrude","SWEPT_FACE",FACE,{"disambiguationData":[OSD([subQ5])]})])],"derivedFrom":makeQuery(id+"F3.boolean.opBoolean","COPY",FACE,{"derivedFrom":makeQuery(id+"F3.opExtrude","CAP_FACE",FACE,{"disambiguationData":[OSD([subQ5,subQ1,subQ6,subQ7,subQ4,subQ3,subQ2,subQ0])],"isStart":false})})}),makeQuery(id+"F8.opExtrude","SWEPT_FACE",FACE,{"disambiguationData":[OSD([sQuery(id+"F7.wireOp",EDGE,"E67")])]})]});}
            var Q5;
            Q5=makeQuery(id+"F8.boolean.opBoolean","INTERSECT",EDGE,{"disambiguationData":[OD(0.0)],"derivedFrom":[makeQuery(id+"F5.opExtrude","SWEPT_FACE",FACE,{"disambiguationData":[OSD([sQuery(id+"F4.wireOp",EDGE,"E30")])]}),makeQuery(id+"F8.opExtrude","SWEPT_FACE",FACE,{"disambiguationData":[OSD([sQuery(id+"F7.wireOp",EDGE,"E67")])]})]});
            fillet(context, id + "F14", {"entities" : qUnion([Q0, Q1, Q2, Q3, Q4, Q5]), "radius" : 3 * mm, "tangentPropagation" : true, "allowEdgeOverflow" : false});
        }
        {
            var Q0;
            Q0=makeQuery(id+"F1.opExtrude","CAP_EDGE",EDGE,{"disambiguationData":[OSD([sQuery(id+"F0.wireOp",EDGE,"E1.bottom")])],"isStart":false});
            fillet(context, id + "F15", {"entities" : qUnion([Q0]), "radius" : 2 * mm, "tangentPropagation" : true, "allowEdgeOverflow" : false});
        }
        {
            var Q0;
            {var subQ0=sQuery(id+"F0.wireOp",EDGE,"E22.filletArc");var subQ1=sQuery(id+"F0.wireOp",EDGE,"E7");var subQ2=sQuery(id+"F0.wireOp",EDGE,"E6");var subQ3=sQuery(id+"F0.wireOp",EDGE,"E5");var subQ4=sQuery(id+"F0.wireOp",EDGE,"E4");var subQ5=sQuery(id+"F0.wireOp",EDGE,"E1.bottom");var subQ6=sQuery(id+"F0.wireOp",EDGE,"E21.filletArc");var subQ7=sQuery(id+"F0.wireOp",EDGE,"E1.top");var subQ8=sQuery(id+"F0.wireOp",EDGE,"E1.left");var subQ9=sQuery(id+"F0.wireOp",EDGE,"E1.right");var subQ10=sQuery(id+"F0.wireOp",EDGE,"E23.filletArc");var subQ11=sQuery(id+"F0.wireOp",EDGE,"E24.filletArc");Q0=makeQuery(id+"F2.boolean.opBoolean","SPLIT",FACE,{"disambiguationData":[TD([makeQuery(id+"F1.opExtrude","SWEPT_FACE",FACE,{"disambiguationData":[OSD([subQ5])]})])],"derivedFrom":makeQuery(id+"F1.opExtrude","CAP_FACE",FACE,{"disambiguationData":[OSD([subQ5,subQ7,subQ8,subQ9,subQ4,subQ3,subQ2,subQ1,subQ6,subQ0,subQ10,subQ11])],"isStart":true})});}
            var sketch = newSketch(context, id + "F16", { "sketchPlane" : qUnion([Q0])});
            skPoint(sketch, "E79.0", {"position": v(-60, 38.83) * mm});
            skCircle(sketch, "E80.0", {"center": v(-60, 60) * mm, "radius": 4 * mm});
            skLineSegment(sketch, "E81.0.0", {"start": v(64.25, 74.25) * mm, "end": v(-64.25, 74.25) * mm});
            skArc(sketch, "E81.0.1", {"start": v(-64.25, 74.25) * mm, "mid": v(-71.32, 71.32) * mm, "end": v(-74.25, 64.25) * mm});
            skLineSegment(sketch, "E81.0.2", {"start": v(-74.25, 64.25) * mm, "end": v(-74.25, -64.25) * mm});
            skArc(sketch, "E81.0.3", {"start": v(-74.25, -64.25) * mm, "mid": v(-71.32, -71.32) * mm, "end": v(-64.25, -74.25) * mm});
            skLineSegment(sketch, "E81.0.4", {"start": v(-64.25, -74.25) * mm, "end": v(64.25, -74.25) * mm});
            skArc(sketch, "E81.0.5", {"start": v(64.25, -74.25) * mm, "mid": v(71.32, -71.32) * mm, "end": v(74.25, -64.25) * mm});
            skLineSegment(sketch, "E81.0.6", {"start": v(74.25, -64.25) * mm, "end": v(74.25, 64.25) * mm});
            skArc(sketch, "E81.0.7", {"start": v(74.25, 64.25) * mm, "mid": v(71.32, 71.32) * mm, "end": v(64.25, 74.25) * mm});
            skPoint(sketch, "E82.0", {"position": v(0, 60) * mm});
            skArc(sketch, "E83.0.0", {"start": v(51.7, -42.45) * mm, "mid": v(53.38, -40.97) * mm, "end": v(54, -38.83) * mm});
            skLineSegment(sketch, "E83.0.1", {"start": v(54, -38.83) * mm, "end": v(54, 38.83) * mm});
            skArc(sketch, "E83.0.2", {"start": v(54, 38.83) * mm, "mid": v(53.38, 40.97) * mm, "end": v(51.7, 42.45) * mm});
            skArc(sketch, "E83.0.3", {"start": v(51.7, 42.45) * mm, "mid": v(0, 54) * mm, "end": v(-51.7, 42.45) * mm});
            skArc(sketch, "E83.0.4", {"start": v(-51.7, 42.45) * mm, "mid": v(-53.38, 40.97) * mm, "end": v(-54, 38.83) * mm});
            skLineSegment(sketch, "E83.0.5", {"start": v(-54, 38.83) * mm, "end": v(-54, -38.83) * mm});
            skArc(sketch, "E83.0.6", {"start": v(-54, -38.83) * mm, "mid": v(-53.38, -40.97) * mm, "end": v(-51.7, -42.45) * mm});
            skArc(sketch, "E83.0.7", {"start": v(-51.7, -42.45) * mm, "mid": v(0, -54) * mm, "end": v(51.7, -42.45) * mm});
            skCircle(sketch, "E84.2", {"center": v(-60, -60) * mm, "radius": 4 * mm});
            skArc(sketch, "E85.0", {"start": v(-54.26, -47.88) * mm, "mid": v(0, -60) * mm, "end": v(54.26, -47.88) * mm});
            skArc(sketch, "E85.1", {"start": v(-52.98, -45.17) * mm, "mid": v(0, -57) * mm, "end": v(52.98, -45.17) * mm});
            skArc(sketch, "E85.2", {"start": v(-54.26, -47.88) * mm, "mid": v(0, -60) * mm, "end": v(54.26, -47.88) * mm});
            skCircle(sketch, "E85.5", {"center": v(60, -60) * mm, "radius": 4 * mm});
            skCircle(sketch, "E85.7", {"center": v(60, -60) * mm, "radius": 4 * mm});
            skArc(sketch, "E85.8", {"start": v(52.98, -45.17) * mm, "mid": v(0, -57) * mm, "end": v(-52.98, -45.17) * mm});
            skCircle(sketch, "E86.0", {"center": v(60, 60) * mm, "radius": 4 * mm});
            skLineSegment(sketch, "E87", {"start": v(0, 74.25) * mm, "end": v(0, 104.25) * mm, "construction": true});
            skPoint(sketch, "E87.endSnap0", {"position": v(0, 74.25) * mm});
            skCircle(sketch, "E88", {"center": v(0, 104.25) * mm, "radius": 7.5 * mm});
            skLineSegment(sketch, "E89", {"start": v(33, 74.25) * mm, "end": v(15, 92.25) * mm});
            skLineSegment(sketch, "E90", {"start": v(-33, 74.25) * mm, "end": v(-15, 92.25) * mm});
            skLineSegment(sketch, "E91", {"start": v(-15, 92.25) * mm, "end": v(-15, 104.25) * mm});
            skLineSegment(sketch, "E92", {"start": v(15, 104.25) * mm, "end": v(15, 92.25) * mm});
            skArc(sketch, "E93", {"start": v(15, 104.25) * mm, "mid": v(0, 119.25) * mm, "end": v(-15, 104.25) * mm});
            skLineSegment(sketch, "E94", {"start": v(0, 0) * mm, "end": v(10.12, 0) * mm});
            skLineSegment(sketch, "E95.MirrorCS", {"start": v(15, 92.25) * mm, "end": v(15, 104.25) * mm});
            skArc(sketch, "E96.MirrorCS", {"start": v(-15, 104.25) * mm, "mid": v(0, 119.25) * mm, "end": v(15, 104.25) * mm});
            skLineSegment(sketch, "E97.MirrorCS", {"start": v(-33, -74.25) * mm, "end": v(-15, -92.25) * mm});
            skLineSegment(sketch, "E98.MirrorCS", {"start": v(-15, -92.25) * mm, "end": v(-15, -104.25) * mm});
            skArc(sketch, "E99.MirrorCS", {"start": v(-15, -104.25) * mm, "mid": v(0, -119.25) * mm, "end": v(15, -104.25) * mm});
            skCircle(sketch, "E100.MirrorC", {"center": v(0, -104.25) * mm, "radius": 7.5 * mm});
            skLineSegment(sketch, "E101.MirrorCS", {"start": v(15, -92.25) * mm, "end": v(15, -104.25) * mm});
            skLineSegment(sketch, "E102.MirrorCS", {"start": v(33, -74.25) * mm, "end": v(15, -92.25) * mm});
            skLineSegment(sketch, "E103.MirrorCS", {"start": v(0, -74.25) * mm, "end": v(0, -104.25) * mm, "construction": true});
            skSolve(sketch);
        }
        {
            var Q0;
            Q0=makeQuery(id+"F16.imprint","IMPRINT",FACE,{"disambiguationData":[TD([[makeQuery(id+"F16.imprint","IMPRINT",EDGE,{"derivedFrom":sQuery(id+"F16.wireOp",EDGE,"E88")}),-1.0]])]});
            var Q1;
            {var subQ0=sQuery(id+"F16.wireOp",EDGE,"E97.MirrorCS");Q1=makeQuery(id+"F16.imprint","IMPRINT",FACE,{"disambiguationData":[TD([[makeQuery(id+"F16.imprint","IMPRINT",EDGE,{"derivedFrom":subQ0}),1.0]])]});}
            var Q2;
            Q2=makeQuery(id+"F16.imprint","IMPRINT",FACE,{"disambiguationData":[TD([[makeQuery(id+"F16.imprint","IMPRINT",EDGE,{"derivedFrom":sQuery(id+"F16.wireOp",EDGE,"E80.0")}),-1.0]])]});
            var Q3;
            Q3=makeQuery(id+"F2.opExtrude","CAP_FACE",FACE,{"disambiguationData":[OSD([sQuery(id+"F0.wireOp",EDGE,"E12"),sQuery(id+"F0.wireOp",EDGE,"E13"),sQuery(id+"F0.wireOp",EDGE,"E14"),sQuery(id+"F0.wireOp",EDGE,"E15"),sQuery(id+"F0.wireOp",EDGE,"E17.filletArc"),sQuery(id+"F0.wireOp",EDGE,"E18.filletArc"),sQuery(id+"F0.wireOp",EDGE,"E19.filletArc"),sQuery(id+"F0.wireOp",EDGE,"E20.filletArc"),sQuery(id+"F0.wireOp",EDGE,"E25.0"),sQuery(id+"F0.wireOp",EDGE,"E25.1"),sQuery(id+"F0.wireOp",EDGE,"E25.2"),sQuery(id+"F0.wireOp",EDGE,"E25.3"),sQuery(id+"F0.wireOp",EDGE,"E25.4"),sQuery(id+"F0.wireOp",EDGE,"E25.5"),sQuery(id+"F0.wireOp",EDGE,"E25.6"),sQuery(id+"F0.wireOp",EDGE,"E25.7")])],"isStart":false});
            extrude(context, id + "F17", {"entities" : qUnion([Q0, Q1, Q2]), "operationType" : NewBodyOperationType.ADD, "endBound" : BoundingType.UP_TO_SURFACE, "endBoundEntityFace" : qUnion([Q3]), "depth" : 25 * mm});
        }
    });
